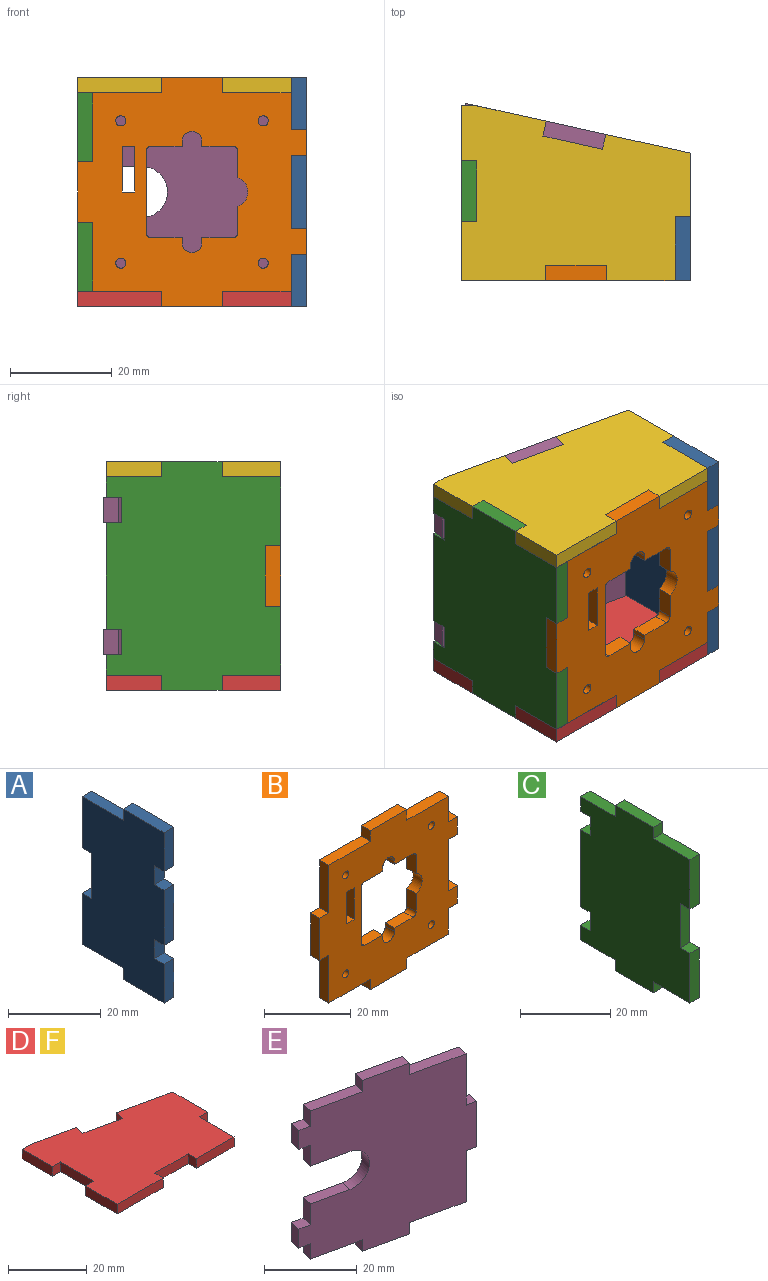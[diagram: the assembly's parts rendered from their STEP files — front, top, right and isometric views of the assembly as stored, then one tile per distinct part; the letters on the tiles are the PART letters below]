
ASSEMBLY  parts=6 mates=5
PART A: 22 faces, bbox 3x25x45 mm
  f0: plane 3x3mm, normal (0,0,-1), area 9mm2, adj f1,f19,f20,f21
  f1: plane 13.5x3mm, normal (0,1,0), area 40.5mm2, adj f0,f2,f20,f21
  f2: plane 12.52x3mm, normal (0,0,1), area 37.6mm2, adj f1,f3,f20,f21
  f3: plane 3x3mm, normal (0,1,0), area 9mm2, adj f2,f4,f20,f21
  f4: plane 12.5x3mm, normal (0,0,1), area 37.5mm2, adj f3,f5,f20,f21
  f5: plane 10.25x3mm, normal (0,-1,0), area 30.7mm2, adj f4,f6,f20,f21
  f6: plane 3x3mm, normal (0,0,-1), area 9mm2, adj f5,f7,f20,f21
  f7: plane 5x3mm, normal (0,-1,0), area 15mm2, adj f6,f8,f20,f21
  f8: plane 3x3mm, normal (0,0,1), area 9mm2, adj f7,f9,f20,f21
  f9: plane 14.5x3mm, normal (0,-1,0), area 43.5mm2, adj f8,f10,f20,f21
  f10: plane 3x3mm, normal (0,0,-1), area 9mm2, adj f9,f11,f20,f21
  f11: plane 5x3mm, normal (0,-1,0), area 15mm2, adj f10,f12,f20,f21
  f12: plane 3x3mm, normal (0,0,1), area 9mm2, adj f11,f13,f20,f21
  f13: plane 10.25x3mm, normal (0,-1,0), area 30.7mm2, adj f12,f14,f20,f21
  f14: plane 12.5x3mm, normal (0,0,-1), area 37.5mm2, adj f13,f15,f20,f21
  f15: plane 3x3mm, normal (0,1,0), area 9mm2, adj f14,f16,f20,f21
  f16: plane 12.52x3mm, normal (0,0,-1), area 37.6mm2, adj f15,f17,f20,f21
  f17: plane 13.5x3mm, normal (0,1,0), area 40.5mm2, adj f16,f18,f20,f21
  f18: plane 3x3mm, normal (0,0,1), area 9mm2, adj f17,f19,f20,f21
  f19: plane 12x3mm, normal (0,1,0), area 36mm2, adj f0,f18,f20,f21
  f20: plane 45x25.02mm, normal (-1,0,0), area 984.9mm2, adj f0,f1,f2,f3,f4,f5,f6,f7
  f21: plane 45x25.02mm, normal (1,0,0), area 984.9mm2, adj f0,f1,f2,f3,f4,f5,f6,f7
PART B: 52 faces, bbox 45x3x45 mm
  f0: cylinder r=1mm len=3mm, axis (0,-1,0), area 4.7mm2, adj f1,f49,f50,f51
  f1: plane 5.17x3mm, normal (-1,0,0), area 15.5mm2, adj f0,f2,f50,f51
  f2: cylinder r=3mm len=5.66mm, axis (0,-1,0), area 22.2mm2, adj f1,f3,f50,f51
  f3: plane 5.17x3mm, normal (-1,0,0), area 15.5mm2, adj f2,f4,f50,f51
  f4: cylinder r=1mm len=3mm, axis (0,-1,0), area 4.7mm2, adj f3,f5,f50,f51
  f5: plane 6.08x3mm, normal (0,0,1), area 18.2mm2, adj f4,f6,f50,f51
  f6: plane 3x1mm, normal (-1,0,0), area 3mm2, adj f5,f7,f50,f51
  f7: cylinder r=1.92mm len=3.85mm, axis (0,-1,0), area 18.1mm2, adj f6,f8,f50,f51
  f8: plane 3x1mm, normal (1,0,0), area 3mm2, adj f7,f9,f50,f51
  f9: plane 6.08x3mm, normal (0,0,1), area 18.2mm2, adj f8,f10,f50,f51
  f10: cylinder r=1mm len=3mm, axis (0,-1,0), area 4.7mm2, adj f9,f11,f50,f51
  f11: plane 16x3mm, normal (1,0,0), area 48mm2, adj f10,f12,f50,f51
  f12: cylinder r=1mm len=3mm, axis (0,-1,0), area 4.7mm2, adj f11,f13,f50,f51
  f13: plane 6.08x3mm, normal (0,0,-1), area 18.2mm2, adj f12,f14,f50,f51
  f14: plane 3x1mm, normal (1,0,0), area 3mm2, adj f13,f15,f50,f51
  f15: cylinder r=1.92mm len=3.85mm, axis (0,-1,0), area 18.1mm2, adj f14,f16,f50,f51
  f16: plane 3x1mm, normal (-1,0,0), area 3mm2, adj f15,f49,f50,f51
  f17: plane 9x3mm, normal (1,0,0), area 27mm2, adj f18,f47,f50,f51
  f18: plane 3x2.5mm, normal (0,0,-1), area 7.5mm2, adj f17,f19,f50,f51
  f19: plane 9x3mm, normal (-1,0,0), area 27mm2, adj f18,f47,f50,f51
  f20: plane 3x3mm, normal (0,0,-1), area 9mm2, adj f21,f48,f50,f51
  f21: plane 13.5x3mm, normal (-1,0,0), area 40.5mm2, adj f20,f22,f50,f51
  f22: plane 13.5x3mm, normal (0,0,-1), area 40.5mm2, adj f21,f23,f50,f51
  f23: plane 3x3mm, normal (-1,0,0), area 9mm2, adj f22,f24,f50,f51
  f24: plane 12x3mm, normal (0,0,-1), area 36mm2, adj f23,f25,f50,f51
  f25: plane 3x3mm, normal (1,0,0), area 9mm2, adj f24,f26,f50,f51
  f26: plane 13.5x3mm, normal (0,0,-1), area 40.5mm2, adj f25,f27,f50,f51
  f27: plane 7.25x3mm, normal (1,0,0), area 21.8mm2, adj f26,f28,f50,f51
  f28: plane 3x3mm, normal (0,0,-1), area 9mm2, adj f27,f29,f50,f51
  f29: plane 5x3mm, normal (1,0,0), area 15mm2, adj f28,f30,f50,f51
  f30: plane 3x3mm, normal (0,0,1), area 9mm2, adj f29,f31,f50,f51
  f31: plane 14.5x3mm, normal (1,0,0), area 43.5mm2, adj f30,f32,f50,f51
  f32: plane 3x3mm, normal (0,0,-1), area 9mm2, adj f31,f33,f50,f51
  f33: plane 5x3mm, normal (1,0,0), area 15mm2, adj f32,f34,f50,f51
  f34: plane 3x3mm, normal (0,0,1), area 9mm2, adj f33,f35,f50,f51
  f35: plane 7.25x3mm, normal (1,0,0), area 21.7mm2, adj f34,f36,f50,f51
  f36: plane 13.5x3mm, normal (0,0,1), area 40.5mm2, adj f35,f37,f50,f51
  f37: plane 3x3mm, normal (1,0,0), area 9mm2, adj f36,f38,f50,f51
  f38: plane 12x3mm, normal (0,0,1), area 36mm2, adj f37,f39,f50,f51
  f39: plane 3x3mm, normal (-1,0,0), area 9mm2, adj f38,f40,f50,f51
  f40: plane 13.5x3mm, normal (0,0,1), area 40.5mm2, adj f39,f41,f50,f51
  f41: plane 13.5x3mm, normal (-1,0,0), area 40.5mm2, adj f40,f42,f50,f51
  f42: plane 3x3mm, normal (0,0,1), area 9mm2, adj f41,f48,f50,f51
  f43: cylinder r=1mm len=3mm, axis (0,-1,0), area 18.8mm2, adj f50,f51
  f44: cylinder r=1mm len=3mm, axis (0,-1,0), area 18.8mm2, adj f50,f51
  f45: cylinder r=1mm len=3mm, axis (0,-1,0), area 18.8mm2, adj f50,f51
  f46: cylinder r=1mm len=3mm, axis (0,-1,0), area 18.8mm2, adj f50,f51
  f47: plane 3x2.5mm, normal (0,0,1), area 7.5mm2, adj f17,f19,f50,f51
  f48: plane 12x3mm, normal (-1,0,0), area 36mm2, adj f20,f42,f50,f51
  f49: plane 6.08x3mm, normal (0,0,-1), area 18.2mm2, adj f0,f16,f50,f51
  f50: plane 45x45mm, normal (0,1,0), area 1273.2mm2, adj f0,f1,f2,f3,f4,f5,f6,f7
  f51: plane 45x45mm, normal (0,-1,0), area 1273.2mm2, adj f0,f1,f2,f3,f4,f5,f6,f7
PART C: 26 faces, bbox 3x34.3x45 mm
  f0: plane 3x3mm, normal (0,0,-1), area 9mm2, adj f1,f23,f24,f25
  f1: plane 13.5x3mm, normal (0,-1,0), area 40.5mm2, adj f0,f2,f24,f25
  f2: plane 11.5x3mm, normal (0,0,1), area 34.5mm2, adj f1,f3,f24,f25
  f3: plane 3x3mm, normal (0,-1,0), area 9mm2, adj f2,f4,f24,f25
  f4: plane 12x3mm, normal (0,0,1), area 36mm2, adj f3,f5,f24,f25
  f5: plane 3x3mm, normal (0,1,0), area 9mm2, adj f4,f6,f24,f25
  f6: plane 10.84x3mm, normal (0,0,1), area 32.5mm2, adj f5,f7,f24,f25
  f7: plane 4x3mm, normal (0,1,0), area 12mm2, adj f6,f8,f24,f25
  f8: plane 3x3mm, normal (0,0,-1), area 9mm2, adj f7,f9,f24,f25
  f9: plane 5x3mm, normal (0,1,0), area 15mm2, adj f8,f10,f24,f25
  f10: plane 3x3mm, normal (0,0,1), area 9mm2, adj f9,f11,f24,f25
  f11: plane 21x3mm, normal (0,1,0), area 63mm2, adj f10,f12,f24,f25
  f12: plane 3x3mm, normal (0,0,-1), area 9mm2, adj f11,f13,f24,f25
  f13: plane 5x3mm, normal (0,1,0), area 15mm2, adj f12,f14,f24,f25
  f14: plane 3x3mm, normal (0,0,1), area 9mm2, adj f13,f15,f24,f25
  f15: plane 4x3mm, normal (0,1,0), area 12mm2, adj f14,f16,f24,f25
  f16: plane 10.84x3mm, normal (0,0,-1), area 32.5mm2, adj f15,f17,f24,f25
  f17: plane 3x3mm, normal (0,1,0), area 9mm2, adj f16,f18,f24,f25
  f18: plane 12x3mm, normal (0,0,-1), area 36mm2, adj f17,f19,f24,f25
  f19: plane 3x3mm, normal (0,-1,0), area 9mm2, adj f18,f20,f24,f25
  f20: plane 11.5x3mm, normal (0,0,-1), area 34.5mm2, adj f19,f21,f24,f25
  f21: plane 13.5x3mm, normal (0,-1,0), area 40.5mm2, adj f20,f22,f24,f25
  f22: plane 3x3mm, normal (0,0,1), area 9mm2, adj f21,f23,f24,f25
  f23: plane 12x3mm, normal (0,-1,0), area 36mm2, adj f0,f22,f24,f25
  f24: plane 45x34.34mm, normal (1,0,0), area 1345.1mm2, adj f0,f1,f2,f3,f4,f5,f6,f7
  f25: plane 45x34.34mm, normal (-1,0,0), area 1345.1mm2, adj f0,f1,f2,f3,f4,f5,f6,f7
PART D: 21 faces, bbox 45x34.3x3 mm
  f0: plane 3x3mm, normal (0,1,0), area 9mm2, adj f1,f18,f19,f20
  f1: plane 10.84x3mm, normal (-1,0,0), area 32.5mm2, adj f0,f2,f19,f20
  f2: plane 3x3mm, normal (0,-1,0), area 9mm2, adj f1,f3,f19,f20
  f3: plane 12x3mm, normal (-1,0,0), area 36mm2, adj f2,f4,f19,f20
  f4: plane 3x3mm, normal (0,1,0), area 9mm2, adj f3,f5,f19,f20
  f5: plane 11.5x3mm, normal (-1,0,0), area 34.5mm2, adj f4,f6,f19,f20
  f6: plane 16.5x3mm, normal (0,-1,0), area 49.5mm2, adj f5,f7,f19,f20
  f7: plane 3x3mm, normal (1,0,0), area 9mm2, adj f6,f8,f19,f20
  f8: plane 12x3mm, normal (0,-1,0), area 36mm2, adj f7,f9,f19,f20
  f9: plane 3x3mm, normal (-1,0,0), area 9mm2, adj f8,f10,f19,f20
  f10: plane 13.5x3mm, normal (0,-1,0), area 40.5mm2, adj f9,f11,f19,f20
  f11: plane 12.5x3mm, normal (1,0,0), area 37.5mm2, adj f10,f12,f19,f20
  f12: plane 3x3mm, normal (0,-1,0), area 9mm2, adj f11,f13,f19,f20
  f13: plane 12.52x3mm, normal (1,0,0), area 37.6mm2, adj f12,f14,f19,f20
  f14: plane 16.64x3.69mm, normal (0.22,0.98,0), area 51.1mm2, adj f13,f15,f19,f20
  f15: plane 3x2.93mm, normal (-0.98,0.22,0), area 9mm2, adj f14,f16,f19,f20
  f16: plane 11.72x3mm, normal (0.22,0.98,0), area 36mm2, adj f15,f17,f19,f20
  f17: plane 3x2.93mm, normal (0.98,-0.22,0), area 9mm2, adj f16,f18,f19,f20
  f18: plane 13.64x3.02mm, normal (0.22,0.98,0), area 41.9mm2, adj f0,f17,f19,f20
  f19: plane 45x34.34mm, normal (0,0,1), area 1204mm2, adj f0,f1,f2,f3,f4,f5,f6,f7
  f20: plane 45x34.34mm, normal (0,0,-1), area 1204mm2, adj f0,f1,f2,f3,f4,f5,f6,f7
PART E: 30 faces, bbox 44.9x12.7x45 mm
  f0: plane 13.5x2.93mm, normal (0.98,-0.22,0), area 40.5mm2, adj f1,f27,f28,f29
  f1: plane 3.51x3.29mm, normal (0,0,1), area 8.1mm2, adj f0,f2,f28,f29
  f2: plane 12x2.93mm, normal (0.98,-0.22,0), area 36mm2, adj f1,f3,f28,f29
  f3: plane 3.51x3.29mm, normal (0,0,-1), area 8.1mm2, adj f2,f4,f28,f29
  f4: plane 13.5x2.93mm, normal (0.98,-0.22,0), area 40.5mm2, adj f3,f5,f28,f29
  f5: plane 14.66x6.03mm, normal (0,0,-1), area 43mm2, adj f4,f6,f28,f29
  f6: plane 3x2.93mm, normal (0.98,-0.22,0), area 9mm2, adj f5,f7,f28,f29
  f7: plane 12.37x5.53mm, normal (0,0,-1), area 36mm2, adj f6,f8,f28,f29
  f8: plane 3x2.93mm, normal (-0.98,0.22,0), area 9mm2, adj f7,f9,f28,f29
  f9: plane 13.63x5.81mm, normal (0,0,-1), area 39.9mm2, adj f8,f10,f28,f29
  f10: plane 4x2.93mm, normal (-0.98,0.22,0), area 12mm2, adj f9,f11,f28,f29
  f11: plane 3.58x3.58mm, normal (0,0,-1), area 9mm2, adj f10,f12,f28,f29
  f12: plane 5x2.93mm, normal (-0.98,0.22,0), area 15mm2, adj f11,f13,f28,f29
  f13: plane 3.58x3.58mm, normal (0,0,1), area 9mm2, adj f12,f14,f28,f29
  f14: plane 5.5x2.93mm, normal (-0.98,0.22,0), area 16.5mm2, adj f13,f15,f28,f29
  f15: plane 10.41x5.09mm, normal (0,0,1), area 30mm2, adj f14,f16,f28,f29
  f16: cylinder r=5mm len=10mm, axis (0.22,0.98,0), area 47.1mm2, adj f15,f17,f28,f29
  f17: plane 10.41x5.09mm, normal (0,0,-1), area 30mm2, adj f16,f18,f28,f29
  f18: plane 5.5x2.93mm, normal (-0.98,0.22,0), area 16.5mm2, adj f17,f19,f28,f29
  f19: plane 3.58x3.58mm, normal (0,0,-1), area 9mm2, adj f18,f20,f28,f29
  f20: plane 5x2.93mm, normal (-0.98,0.22,0), area 15mm2, adj f19,f21,f28,f29
  f21: plane 3.58x3.58mm, normal (0,0,1), area 9mm2, adj f20,f22,f28,f29
  f22: plane 4x2.93mm, normal (-0.98,0.22,0), area 12mm2, adj f21,f23,f28,f29
  f23: plane 13.63x5.81mm, normal (0,0,1), area 39.9mm2, adj f22,f24,f28,f29
  f24: plane 3x2.93mm, normal (-0.98,0.22,0), area 9mm2, adj f23,f25,f28,f29
  f25: plane 12.37x5.53mm, normal (0,0,1), area 36mm2, adj f24,f26,f28,f29
  f26: plane 3x2.93mm, normal (0.98,-0.22,0), area 9mm2, adj f25,f27,f28,f29
  f27: plane 14.66x6.03mm, normal (0,0,1), area 43mm2, adj f0,f26,f28,f29
  f28: plane 45x44.27mm, normal (-0.22,-0.98,0), area 1541.3mm2, adj f0,f1,f2,f3,f4,f5,f6,f7
  f29: plane 45x44.27mm, normal (0.22,0.98,0), area 1541.3mm2, adj f0,f1,f2,f3,f4,f5,f6,f7
PART F: same geometry as D
PLACE A t=(2.82,1.64,3.98)mm
PLACE B t=(2.82,1.64,3.98)mm
PLACE C t=(2.82,1.64,3.98)mm
PLACE D t=(2.82,1.64,-38.02)mm
PLACE E t=(2.82,1.64,3.98)mm
PLACE F t=(2.82,1.64,3.98)mm fixed
MATE fastened C.f25 <-> F.f1  axis (-1,0,0) through (2.82,25.14,6.98)mm
MATE fastened D.f20 <-> C.f18  axis (0,0,-1) through (2.82,13.14,-38.02)mm
MATE fastened E.f25 <-> F.f19  axis (0,0,1) through (18.82,30.02,6.98)mm
MATE fastened B.f51 <-> F.f10  axis (0,-1,0) through (31.32,1.64,6.98)mm
MATE fastened A.f21 <-> F.f13  axis (1,0,0) through (47.82,14.14,6.98)mm
